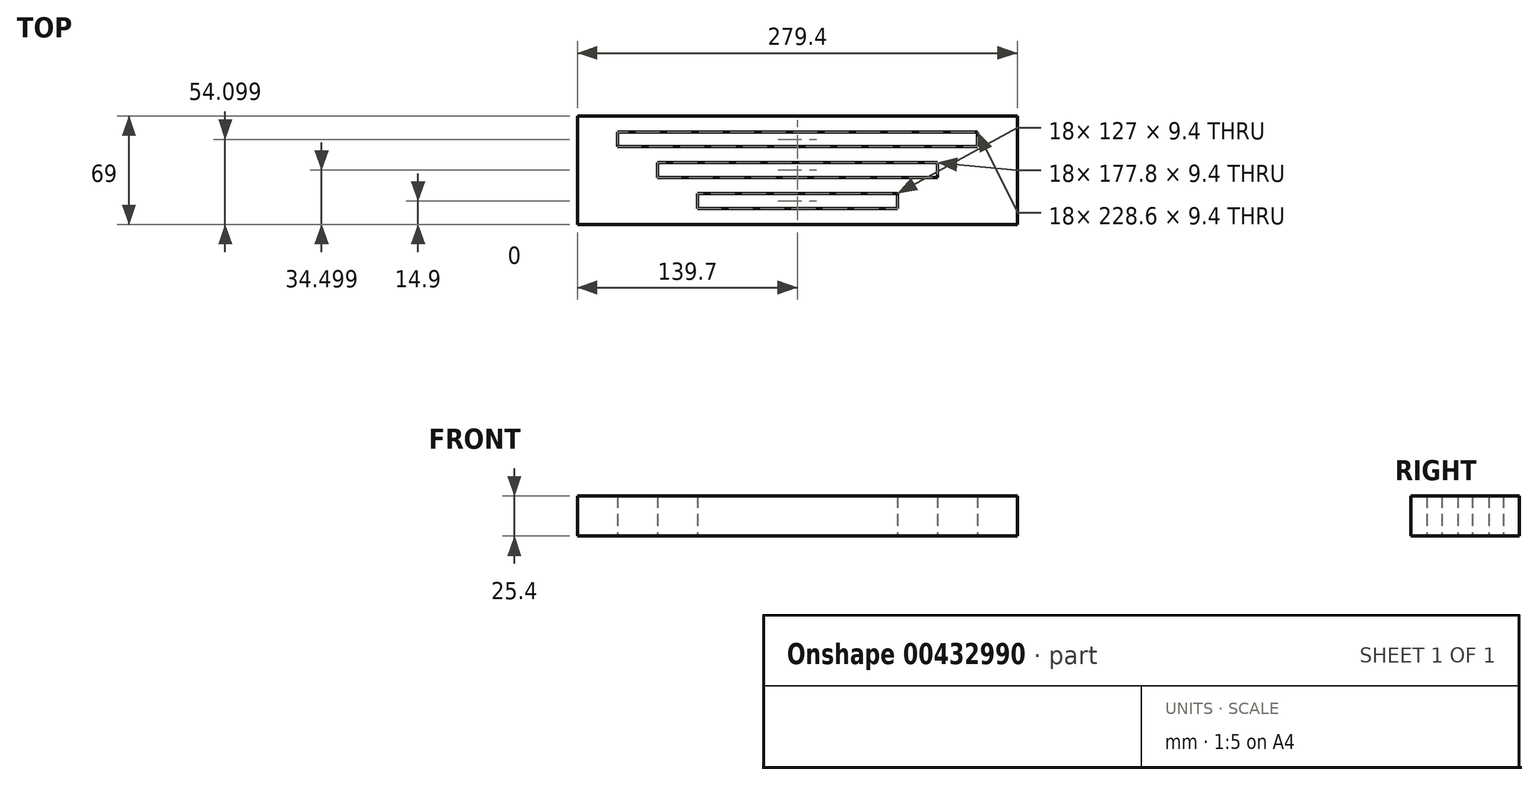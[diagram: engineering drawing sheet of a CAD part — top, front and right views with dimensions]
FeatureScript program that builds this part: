
annotation { "Feature Type Name" : "Feature", "Feature Type Description" : "" }
export const myFeature = defineFeature(function(context is Context, id is Id, definition is map)
    precondition{}
    {
        {
            var Q0;
            Q0=qCreatedBy(makeId("Top.planeOp"),FACE);
            var sketch = newSketch(context, id + "F0", { "sketchPlane" : qUnion([Q0])});
            skLineSegment(sketch, "E0.bottom", {"start": v(-61, 39.2) * mm, "end": v(218.4, 39.2) * mm});
            skLineSegment(sketch, "E0.top", {"start": v(-61, -29.8) * mm, "end": v(218.4, -29.8) * mm});
            skLineSegment(sketch, "E0.left", {"start": v(-61, 39.2) * mm, "end": v(-61, -29.8) * mm});
            skLineSegment(sketch, "E0.right", {"start": v(218.4, 39.2) * mm, "end": v(218.4, -29.8) * mm});
            skLineSegment(sketch, "E1.bottom", {"start": v(-35.6, 29) * mm, "end": v(193, 29) * mm});
            skLineSegment(sketch, "E1.top", {"start": v(-35.6, 19.6) * mm, "end": v(193, 19.6) * mm});
            skLineSegment(sketch, "E1.left", {"start": v(-35.6, 29) * mm, "end": v(-35.6, 19.6) * mm});
            skLineSegment(sketch, "E1.right", {"start": v(193, 29) * mm, "end": v(193, 19.6) * mm});
            skLineSegment(sketch, "E2.bottom", {"start": v(-10.2, 9.4) * mm, "end": v(167.6, 9.4) * mm});
            skLineSegment(sketch, "E2.top", {"start": v(-10.2, 0) * mm, "end": v(167.6, 0) * mm});
            skLineSegment(sketch, "E2.left", {"start": v(-10.2, 9.4) * mm, "end": v(-10.2, 0) * mm});
            skLineSegment(sketch, "E2.right", {"start": v(167.6, 9.4) * mm, "end": v(167.6, 0) * mm});
            skLineSegment(sketch, "E3.bottom", {"start": v(15.2, -10.2) * mm, "end": v(142.2, -10.2) * mm});
            skLineSegment(sketch, "E3.top", {"start": v(15.2, -19.6) * mm, "end": v(142.2, -19.6) * mm});
            skLineSegment(sketch, "E3.left", {"start": v(15.2, -10.2) * mm, "end": v(15.2, -19.6) * mm});
            skLineSegment(sketch, "E3.right", {"start": v(142.2, -10.2) * mm, "end": v(142.2, -19.6) * mm});
            skLineSegment(sketch, "E4", {"start": v(78.7, 39.2) * mm, "end": v(78.7, 29) * mm, "construction": true});
            skPoint(sketch, "E4.endSnap0", {"position": v(78.7, 29) * mm});
            skLineSegment(sketch, "E5", {"start": v(78.7, 19.6) * mm, "end": v(78.7, 9.4) * mm, "construction": true});
            skPoint(sketch, "E5.endSnap0", {"position": v(78.7, 9.4) * mm});
            skLineSegment(sketch, "E6", {"start": v(78.7, 0) * mm, "end": v(78.7, -10.2) * mm, "construction": true});
            skLineSegment(sketch, "E7", {"start": v(78.7, -19.6) * mm, "end": v(78.7, -29.8) * mm, "construction": true});
            skSolve(sketch);
        }
        {
            var Q0;
            Q0 = qSketchRegion(id + "F0", true);
            extrude(context, id + "F1", {"entities" : qUnion([Q0]), "depth" : 25.4 * mm});
        }
    });
